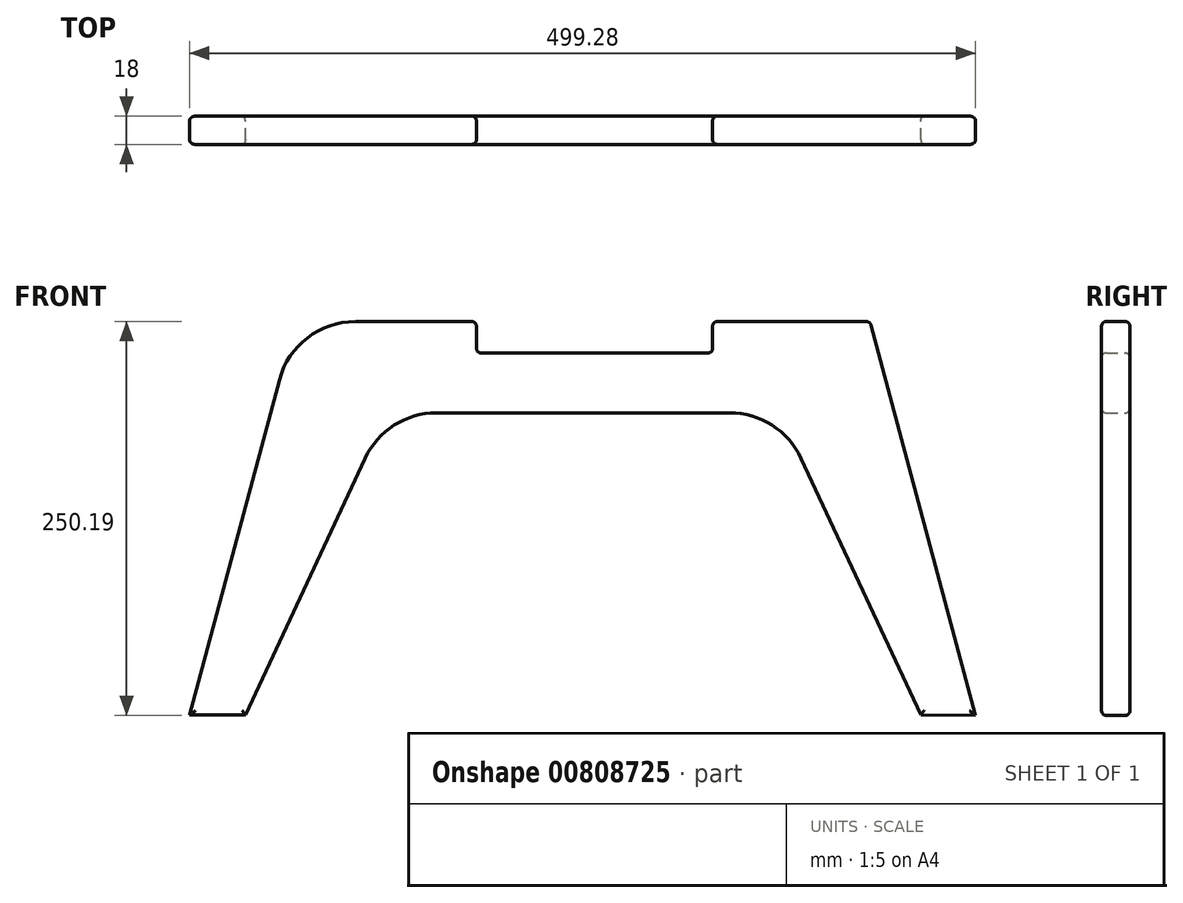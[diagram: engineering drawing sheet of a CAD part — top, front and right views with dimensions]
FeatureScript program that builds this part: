
annotation { "Feature Type Name" : "Feature", "Feature Type Description" : "" }
export const myFeature = defineFeature(function(context is Context, id is Id, definition is map)
    precondition{}
    {
        {
            var Q0;
            Q0=qCreatedBy(makeId("Front.planeOp"),FACE);
            var sketch = newSketch(context, id + "F0", { "sketchPlane" : qUnion([Q0])});
            skLineSegment(sketch, "E0", {"start": v(0, 0) * mm, "end": v(57.06, 212.94) * mm});
            skLineSegment(sketch, "E1", {"start": v(105.35, 250) * mm, "end": v(178.76, 250) * mm});
            skLineSegment(sketch, "E2", {"start": v(250, 192) * mm, "end": v(156.84, 192) * mm});
            skLineSegment(sketch, "E3", {"start": v(111.53, 163.13) * mm, "end": v(35.46, 0) * mm});
            skLineSegment(sketch, "E4", {"start": v(35.46, 0) * mm, "end": v(0, 0) * mm});
            skLineSegment(sketch, "E5.MirrorCS", {"start": v(250, 192) * mm, "end": v(343.16, 192) * mm});
            skLineSegment(sketch, "E6.MirrorCS", {"start": v(388.47, 163.13) * mm, "end": v(464.54, 0) * mm});
            skLineSegment(sketch, "E7", {"start": v(182.24, 242.73) * mm, "end": v(182.24, 232.73) * mm});
            skLineSegment(sketch, "E8", {"start": v(188.76, 230) * mm, "end": v(329.24, 230) * mm});
            skPoint(sketch, "E9.visualSharp", {"position": v(66.99, 250) * mm});
            skArc(sketch, "E9.filletArc", {"start": v(105.35, 250) * mm, "mid": v(74.92, 239.67) * mm, "end": v(57.06, 212.94) * mm});
            skPoint(sketch, "E10.visualSharp", {"position": v(124.99, 192) * mm});
            skArc(sketch, "E10.filletArc", {"start": v(156.84, 192) * mm, "mid": v(129.98, 184.17) * mm, "end": v(111.53, 163.13) * mm});
            skPoint(sketch, "E11.visualSharp", {"position": v(375.01, 192) * mm});
            skArc(sketch, "E11.filletArc", {"start": v(388.47, 163.13) * mm, "mid": v(370.02, 184.17) * mm, "end": v(343.16, 192) * mm});
            skPoint(sketch, "E12.visualSharp", {"position": v(182.24, 250) * mm});
            skPoint(sketch, "E13.visualSharp", {"position": v(182.24, 230) * mm});
            skPoint(sketch, "E14.visualSharp", {"position": v(437.6, 230) * mm});
            skLineSegment(sketch, "E15", {"start": v(178.76, 250) * mm, "end": v(179.24, 250) * mm});
            skLineSegment(sketch, "E16", {"start": v(182.24, 247) * mm, "end": v(182.24, 242.73) * mm});
            skLineSegment(sketch, "E17", {"start": v(182.24, 232.73) * mm, "end": v(182.24, 230) * mm});
            skLineSegment(sketch, "E18", {"start": v(188.76, 230) * mm, "end": v(182.24, 230) * mm});
            skLineSegment(sketch, "E19", {"start": v(335.24, 250) * mm, "end": v(429.94, 250) * mm});
            skLineSegment(sketch, "E20", {"start": v(332.24, 247) * mm, "end": v(332.24, 233) * mm});
            skPoint(sketch, "E21.start.orphan", {"position": v(432.24, 230) * mm});
            skLineSegment(sketch, "E22", {"start": v(432.83, 247.78) * mm, "end": v(499.28, -0.2) * mm});
            skLineSegment(sketch, "E23", {"start": v(464.54, 0) * mm, "end": v(499.28, -0.2) * mm});
            skArc(sketch, "E24.filletArc", {"start": v(182.24, 247) * mm, "mid": v(181.36, 249.12) * mm, "end": v(179.24, 250) * mm});
            skPoint(sketch, "E25.visualSharp", {"position": v(432.24, 250) * mm});
            skArc(sketch, "E25.filletArc", {"start": v(432.83, 247.78) * mm, "mid": v(431.76, 249.38) * mm, "end": v(429.94, 250) * mm});
            skPoint(sketch, "E26.visualSharp", {"position": v(332.24, 230) * mm});
            skArc(sketch, "E26.filletArc", {"start": v(329.24, 230) * mm, "mid": v(331.36, 230.88) * mm, "end": v(332.24, 233) * mm});
            skPoint(sketch, "E27.visualSharp", {"position": v(332.24, 250) * mm});
            skArc(sketch, "E27.filletArc", {"start": v(335.24, 250) * mm, "mid": v(333.12, 249.12) * mm, "end": v(332.24, 247) * mm});
            skSolve(sketch);
        }
        {
            var Q0;
            Q0=makeQuery(id+"F0.imprint","IMPRINT",FACE,{"disambiguationData":[TD([[makeQuery(id+"F0.imprint","IMPRINT",EDGE,{"derivedFrom":sQuery(id+"F0.wireOp",EDGE,"E0")}),-1.0]])]});
            extrude(context, id + "F1", {"entities" : qUnion([Q0]), "depth" : 18 * mm, "offsetDistance" : 25 * mm});
        }
        {
            var Q0;
            Q0=makeQuery(id+"F1.opExtrude","CAP_FACE",FACE,{"disambiguationData":[OSD([sQuery(id+"F0.wireOp",EDGE,"E0"),sQuery(id+"F0.wireOp",EDGE,"E1"),sQuery(id+"F0.wireOp",EDGE,"E2"),sQuery(id+"F0.wireOp",EDGE,"E3"),sQuery(id+"F0.wireOp",EDGE,"E4"),sQuery(id+"F0.wireOp",EDGE,"E5.MirrorCS"),sQuery(id+"F0.wireOp",EDGE,"E6.MirrorCS"),sQuery(id+"F0.wireOp",EDGE,"89b3835c-9e31-4fd1-bfc9-12b4f815a5230.MirrorCS"),sQuery(id+"F0.wireOp",EDGE,"78e46f3d-e32f-4bbe-bbd1-9f27c767923d0.MirrorCS"),sQuery(id+"F0.wireOp",EDGE,"E7"),sQuery(id+"F0.wireOp",EDGE,"E8"),sQuery(id+"F0.wireOp",EDGE,"E9.filletArc"),sQuery(id+"F0.wireOp",EDGE,"E10.filletArc"),sQuery(id+"F0.wireOp",EDGE,"E11.filletArc"),sQuery(id+"F0.wireOp",EDGE,"E12.filletArc"),sQuery(id+"F0.wireOp",EDGE,"E13.filletArc"),sQuery(id+"F0.wireOp",EDGE,"E14.filletArc")])],"isStart":false});
            var Q1;
            Q1=makeQuery(id+"F1.opExtrude","CAP_FACE",FACE,{"disambiguationData":[OSD([sQuery(id+"F0.wireOp",EDGE,"E0"),sQuery(id+"F0.wireOp",EDGE,"E1"),sQuery(id+"F0.wireOp",EDGE,"E2"),sQuery(id+"F0.wireOp",EDGE,"E3"),sQuery(id+"F0.wireOp",EDGE,"E4"),sQuery(id+"F0.wireOp",EDGE,"E5.MirrorCS"),sQuery(id+"F0.wireOp",EDGE,"E6.MirrorCS"),sQuery(id+"F0.wireOp",EDGE,"89b3835c-9e31-4fd1-bfc9-12b4f815a5230.MirrorCS"),sQuery(id+"F0.wireOp",EDGE,"78e46f3d-e32f-4bbe-bbd1-9f27c767923d0.MirrorCS"),sQuery(id+"F0.wireOp",EDGE,"E7"),sQuery(id+"F0.wireOp",EDGE,"E8"),sQuery(id+"F0.wireOp",EDGE,"E9.filletArc"),sQuery(id+"F0.wireOp",EDGE,"E10.filletArc"),sQuery(id+"F0.wireOp",EDGE,"E11.filletArc"),sQuery(id+"F0.wireOp",EDGE,"E12.filletArc"),sQuery(id+"F0.wireOp",EDGE,"E13.filletArc"),sQuery(id+"F0.wireOp",EDGE,"E14.filletArc")])],"isStart":true});
            var Q2;
            Q2=makeQuery(id+"F1.opExtrude","SWEPT_EDGE",EDGE,{"disambiguationData":[OSD([sQuery(id+"F0.wireOp",EDGE,"E17"),sQuery(id+"F0.wireOp",EDGE,"E18")])]});
            fillet(context, id + "F2", {"entities" : qUnion([Q0, Q1, Q2]), "radius" : 3 * mm, "tangentPropagation" : true, "allowEdgeOverflow" : false});
        }
        {
            var Q0;
            Q0=makeQuery(id+"F1.opExtrude","SWEPT_FACE",FACE,{"disambiguationData":[OSD([sQuery(id+"F0.wireOp",EDGE,"E8"),sQuery(id+"F0.wireOp",EDGE,"E18")])]});
            var sketch = newSketch(context, id + "F3", { "sketchPlane" : qUnion([Q0])});
            skPoint(sketch, "E28", {"position": v(257.24, -9) * mm});
            skPoint(sketch, "E29.orphan", {"position": v(185.24, -9) * mm});
            skPoint(sketch, "E30.end.orphan", {"position": v(329.24, -9) * mm});
            skSolve(sketch);
        }
    });
